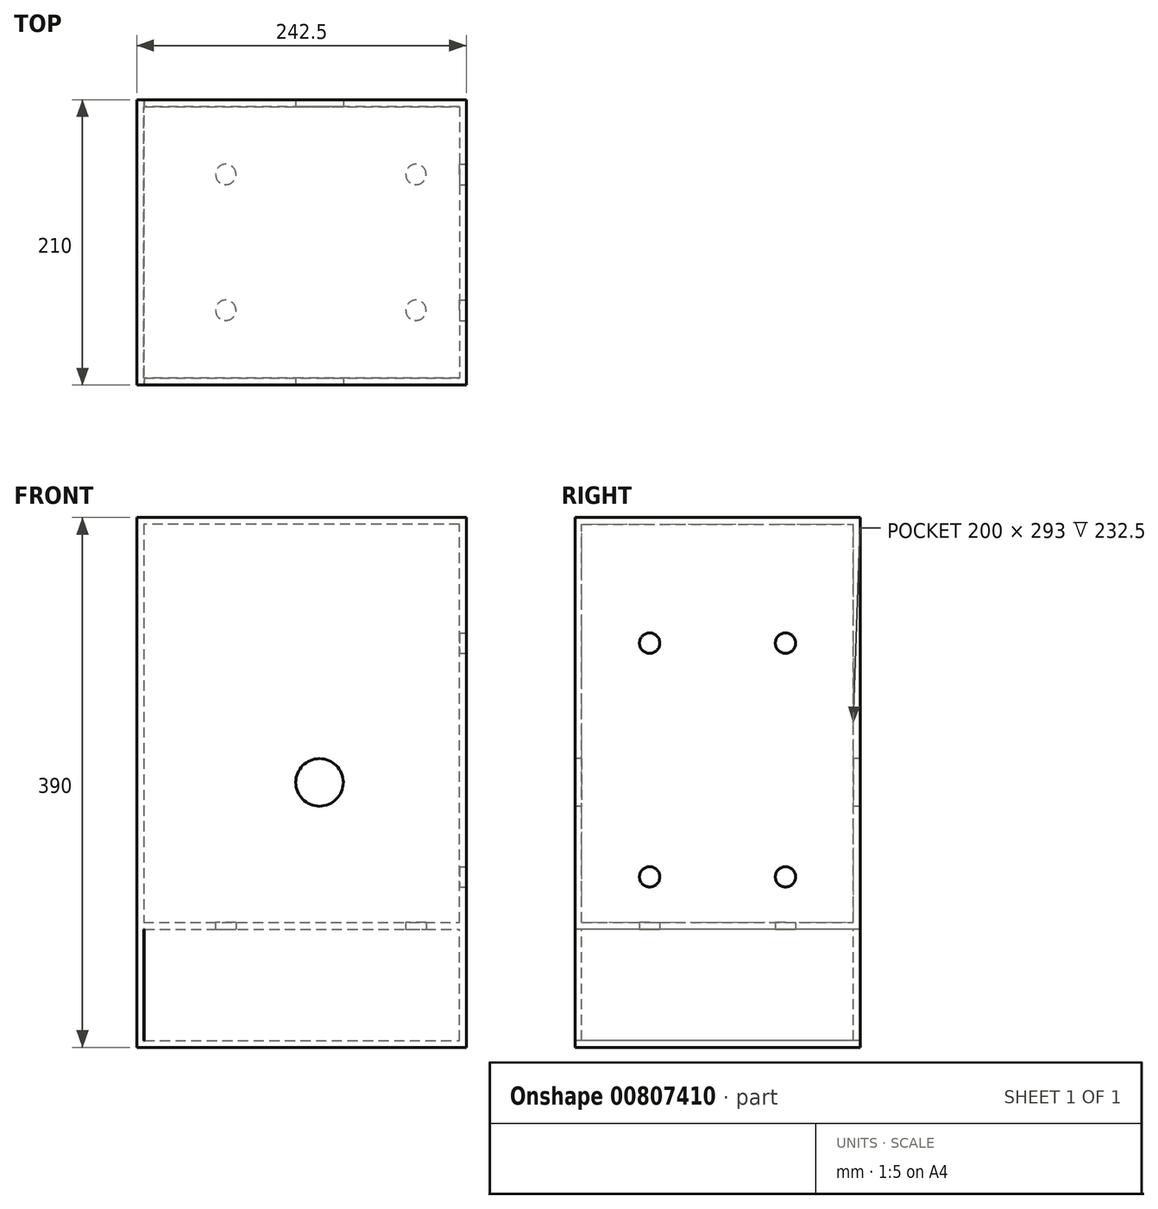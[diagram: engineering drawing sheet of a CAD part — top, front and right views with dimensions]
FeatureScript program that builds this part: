
annotation { "Feature Type Name" : "Feature", "Feature Type Description" : "" }
export const myFeature = defineFeature(function(context is Context, id is Id, definition is map)
    precondition{}
    {
        {
            var Q0;
            Q0=qCreatedBy(makeId("Front.planeOp"),FACE);
            var sketch = newSketch(context, id + "F0", { "sketchPlane" : qUnion([Q0])});
            skLineSegment(sketch, "E0", {"start": v(145.3, 234.57) * mm, "end": v(-87.2, 234.57) * mm});
            skLineSegment(sketch, "E1", {"start": v(-87.2, 234.57) * mm, "end": v(-87.2, -58.43) * mm});
            skLineSegment(sketch, "E2", {"start": v(-87.2, -58.43) * mm, "end": v(145.3, -58.43) * mm});
            skLineSegment(sketch, "E3", {"start": v(145.3, -58.43) * mm, "end": v(145.3, 234.57) * mm});
            skLineSegment(sketch, "E4", {"start": v(-87.2, 234.57) * mm, "end": v(-92.2, 234.57) * mm});
            skLineSegment(sketch, "E5", {"start": v(-92.2, 234.57) * mm, "end": v(-92.2, -63.43) * mm});
            skLineSegment(sketch, "E6", {"start": v(-92.2, -63.43) * mm, "end": v(150.3, -63.43) * mm});
            skLineSegment(sketch, "E7", {"start": v(150.3, -63.43) * mm, "end": v(150.3, 239.57) * mm});
            skLineSegment(sketch, "E8", {"start": v(150.3, 239.57) * mm, "end": v(-92.2, 239.57) * mm});
            skLineSegment(sketch, "E9", {"start": v(-92.2, 239.57) * mm, "end": v(-92.2, 234.57) * mm});
            skSolve(sketch);
        }
        {
            var Q0;
            Q0=makeQuery(id+"F0.imprint","IMPRINT",FACE,{"disambiguationData":[TD([[makeQuery(id+"F0.imprint","IMPRINT",EDGE,{"derivedFrom":sQuery(id+"F0.wireOp",EDGE,"E0")}),-1.0]])]});
            extrude(context, id + "F1", {"entities" : qUnion([Q0]), "depth" : 200 * mm, "offsetDistance" : 25 * mm});
        }
        {
            var Q0;
            Q0=makeQuery(id+"F1.opExtrude","SWEPT_FACE",FACE,{"disambiguationData":[OSD([sQuery(id+"F0.wireOp",EDGE,"E6")])]});
            var sketch = newSketch(context, id + "F2", { "sketchPlane" : qUnion([Q0])});
            skLineSegment(sketch, "E10", {"start": v(-92.2, 200) * mm, "end": v(-92.2, 205) * mm});
            skLineSegment(sketch, "E11", {"start": v(-92.2, 205) * mm, "end": v(150.3, 205) * mm});
            skLineSegment(sketch, "E12", {"start": v(150.3, 205) * mm, "end": v(150.3, 200) * mm});
            skLineSegment(sketch, "E13", {"start": v(-92.2, 0) * mm, "end": v(-92.2, -5) * mm});
            skLineSegment(sketch, "E14", {"start": v(-92.2, -5) * mm, "end": v(150.3, -5) * mm});
            skLineSegment(sketch, "E15", {"start": v(150.3, -5) * mm, "end": v(150.3, 0) * mm});
            skSolve(sketch);
        }
        {
            var Q0;
            Q0=makeQuery(id+"F2.imprint","IMPRINT",FACE,{"disambiguationData":[TD([[makeQuery(id+"F2.imprint","IMPRINT",EDGE,{"derivedFrom":sQuery(id+"F2.wireOp",EDGE,"E10")}),-1.0]])]});
            var Q1;
            Q1=makeQuery(id+"F2.imprint","IMPRINT",FACE,{"disambiguationData":[TD([[makeQuery(id+"F2.imprint","IMPRINT",EDGE,{"derivedFrom":sQuery(id+"F2.wireOp",EDGE,"E13")}),1.0]])]});
            extrude(context, id + "F3", {"entities" : qUnion([Q0, Q1]), "oppositeDirection" : true, "depth" : 303 * mm, "offsetDistance" : 25 * mm});
        }
        {
            var Q0;
            Q0=makeQuery(id+"F1.opExtrude","SWEPT_FACE",FACE,{"disambiguationData":[OSD([sQuery(id+"F0.wireOp",EDGE,"E7")])]});
            var sketch = newSketch(context, id + "F4", { "sketchPlane" : qUnion([Q0])});
            skLineSegment(sketch, "E16", {"start": v(0, 239.57) * mm, "end": v(-50, 239.57) * mm});
            skLineSegment(sketch, "E17", {"start": v(-50, 239.57) * mm, "end": v(-50, -63.43) * mm});
            skLineSegment(sketch, "E18", {"start": v(-50, -63.43) * mm, "end": v(-50, -24.93) * mm});
            skCircle(sketch, "E19", {"center": v(-50, -24.93) * mm, "radius": 7.5 * mm});
            skLineSegment(sketch, "E20", {"start": v(-50, -24.93) * mm, "end": v(-50, 147.07) * mm});
            skCircle(sketch, "E21", {"center": v(-50, 147.07) * mm, "radius": 7.5 * mm});
            skLineSegment(sketch, "E22", {"start": v(-200, 239.57) * mm, "end": v(-150, 239.57) * mm});
            skLineSegment(sketch, "E23", {"start": v(-150, 239.57) * mm, "end": v(-150, -63.43) * mm});
            skLineSegment(sketch, "E24", {"start": v(-150, -63.43) * mm, "end": v(-150, -24.93) * mm});
            skLineSegment(sketch, "E25", {"start": v(-150, -24.93) * mm, "end": v(-150, 147.07) * mm});
            skCircle(sketch, "E26", {"center": v(-150, 147.07) * mm, "radius": 7.5 * mm});
            skCircle(sketch, "E27", {"center": v(-150, -24.93) * mm, "radius": 7.5 * mm});
            skSolve(sketch);
        }
        {
            var Q0;
            Q0 = qSketchRegion(id + "F4", true);
            extrude(context, id + "F5", {"entities" : qUnion([Q0]), "operationType" : NewBodyOperationType.REMOVE, "oppositeDirection" : true, "depth" : 25 * mm, "offsetDistance" : 25 * mm});
        }
        {
            var Q0;
            Q0=makeQuery(id+"F1.opExtrude","SWEPT_FACE",FACE,{"disambiguationData":[OSD([sQuery(id+"F0.wireOp",EDGE,"E6")])]});
            var sketch = newSketch(context, id + "F6", { "sketchPlane" : qUnion([Q0])});
            skLineSegment(sketch, "E28", {"start": v(150.3, 200) * mm, "end": v(150.3, 150) * mm});
            skLineSegment(sketch, "E29", {"start": v(150.3, 150) * mm, "end": v(-86.02, 150) * mm});
            skLineSegment(sketch, "E30", {"start": v(150.3, 0) * mm, "end": v(150.3, 50) * mm});
            skLineSegment(sketch, "E31", {"start": v(150.3, 50) * mm, "end": v(-86.43, 50) * mm});
            skLineSegment(sketch, "E32", {"start": v(150.3, 50) * mm, "end": v(113.3, 50) * mm});
            skLineSegment(sketch, "E33", {"start": v(113.3, 50) * mm, "end": v(-26.7, 50) * mm});
            skLineSegment(sketch, "E34", {"start": v(-26.7, 50) * mm, "end": v(-26.7, 150) * mm});
            skLineSegment(sketch, "E35", {"start": v(-26.7, 150) * mm, "end": v(113.3, 150) * mm});
            skCircle(sketch, "E36", {"center": v(113.3, 150) * mm, "radius": 7.5 * mm});
            skCircle(sketch, "E37", {"center": v(-26.7, 150) * mm, "radius": 7.5 * mm});
            skCircle(sketch, "E38", {"center": v(-26.7, 50) * mm, "radius": 7.5 * mm});
            skCircle(sketch, "E39", {"center": v(113.3, 50) * mm, "radius": 7.5 * mm});
            skSolve(sketch);
        }
        {
            var Q0;
            Q0 = qSketchRegion(id + "F6", true);
            extrude(context, id + "F7", {"entities" : qUnion([Q0]), "operationType" : NewBodyOperationType.REMOVE, "oppositeDirection" : true, "depth" : 25 * mm, "offsetDistance" : 25 * mm});
        }
        {
            var Q0;
            Q0=makeQuery(id+"F3.opExtrude","SWEPT_FACE",FACE,{"disambiguationData":[OSD([sQuery(id+"F2.wireOp",EDGE,"E11")])]});
            var sketch = newSketch(context, id + "F8", { "sketchPlane" : qUnion([Q0])});
            skLineSegment(sketch, "E40", {"start": v(150.3, -63.43) * mm, "end": v(42.3, -63.43) * mm});
            skLineSegment(sketch, "E41", {"start": v(42.3, -63.43) * mm, "end": v(42.3, 44.57) * mm});
            skCircle(sketch, "E42", {"center": v(42.3, 44.57) * mm, "radius": 17.5 * mm});
            skSolve(sketch);
        }
        {
            var Q0;
            Q0 = qSketchRegion(id + "F8", true);
            extrude(context, id + "F9", {"entities" : qUnion([Q0]), "operationType" : NewBodyOperationType.REMOVE, "endBound" : BoundingType.THROUGH_ALL, "oppositeDirection" : true, "depth" : 400 * mm, "offsetDistance" : 25 * mm});
        }
        {
            var Q0;
            Q0=makeQuery(id+"F3.opExtrude","SWEPT_FACE",FACE,{"disambiguationData":[OSD([sQuery(id+"F2.wireOp",EDGE,"E11")])]});
            var sketch = newSketch(context, id + "F10", { "sketchPlane" : qUnion([Q0])});
            skLineSegment(sketch, "E43", {"start": v(42.3, 44.57) * mm, "end": v(42.3, 239.57) * mm});
            skLineSegment(sketch, "E44", {"start": v(42.3, 44.57) * mm, "end": v(42.3, -150.43) * mm});
            skLineSegment(sketch, "E45", {"start": v(42.3, -150.43) * mm, "end": v(150.3, -150.43) * mm});
            skLineSegment(sketch, "E46", {"start": v(150.3, -150.43) * mm, "end": v(150.3, -63.43) * mm});
            skLineSegment(sketch, "E47", {"start": v(150.3, -63.43) * mm, "end": v(-92.2, -63.43) * mm});
            skLineSegment(sketch, "E48", {"start": v(-92.2, -63.43) * mm, "end": v(-92.2, -150.43) * mm});
            skLineSegment(sketch, "E49", {"start": v(-92.2, -150.43) * mm, "end": v(42.3, -150.43) * mm});
            skLineSegment(sketch, "E50", {"start": v(-92.2, -63.43) * mm, "end": v(-87.2, -63.43) * mm});
            skLineSegment(sketch, "E51", {"start": v(-87.2, -63.43) * mm, "end": v(-87.2, -145.43) * mm});
            skLineSegment(sketch, "E52", {"start": v(-87.2, -145.43) * mm, "end": v(145.3, -145.43) * mm});
            skLineSegment(sketch, "E53", {"start": v(145.3, -145.43) * mm, "end": v(145.3, -63.43) * mm});
            skSolve(sketch);
        }
        {
            var Q0;
            {var subQ1=sQuery(id+"F10.wireOp",EDGE,"E45");Q0=makeQuery(id+"F10.imprint","IMPRINT",FACE,{"disambiguationData":[TD([[makeQuery(id+"F10.imprint","IMPRINT",EDGE,{"derivedFrom":subQ1}),1.0]])]});}
            var Q1;
            Q1=makeQuery(id+"F10.imprint","IMPRINT",FACE,{"disambiguationData":[TD([[makeQuery(id+"F10.imprint","IMPRINT",EDGE,{"derivedFrom":sQuery(id+"F10.wireOp",EDGE,"E48")}),1.0]])]});
            extrude(context, id + "F11", {"entities" : qUnion([Q0, Q1]), "operationType" : NewBodyOperationType.ADD, "oppositeDirection" : true, "depth" : 210 * mm, "offsetDistance" : 25 * mm});
        }
        {
            var Q0;
            Q0=makeQuery(id+"F11.opExtrude","SWEPT_FACE",FACE,{"disambiguationData":[OSD([sQuery(id+"F10.wireOp",EDGE,"E53")])]});
            var sketch = newSketch(context, id + "F12", { "sketchPlane" : qUnion([Q0])});
            skLineSegment(sketch, "E54", {"start": v(205, -145.43) * mm, "end": v(200, -145.43) * mm});
            skLineSegment(sketch, "E55", {"start": v(200, -145.43) * mm, "end": v(200, -63.43) * mm});
            skLineSegment(sketch, "E56", {"start": v(-5, -145.43) * mm, "end": v(0, -145.43) * mm});
            skLineSegment(sketch, "E57", {"start": v(0, -145.43) * mm, "end": v(0, -63.43) * mm});
            skSolve(sketch);
        }
        {
            var Q0;
            Q0=makeQuery(id+"F12.imprint","IMPRINT",FACE,{"disambiguationData":[TD([[makeQuery(id+"F12.imprint","IMPRINT",EDGE,{"derivedFrom":sQuery(id+"F12.wireOp",EDGE,"E56")}),1.0]])]});
            var Q1;
            Q1=makeQuery(id+"F12.imprint","IMPRINT",FACE,{"disambiguationData":[TD([[makeQuery(id+"F12.imprint","IMPRINT",EDGE,{"derivedFrom":sQuery(id+"F12.wireOp",EDGE,"E54")}),1.0]])]});
            extrude(context, id + "F13", {"entities" : qUnion([Q0, Q1]), "operationType" : NewBodyOperationType.ADD, "depth" : 232 * mm, "offsetDistance" : 25 * mm});
        }
    });
